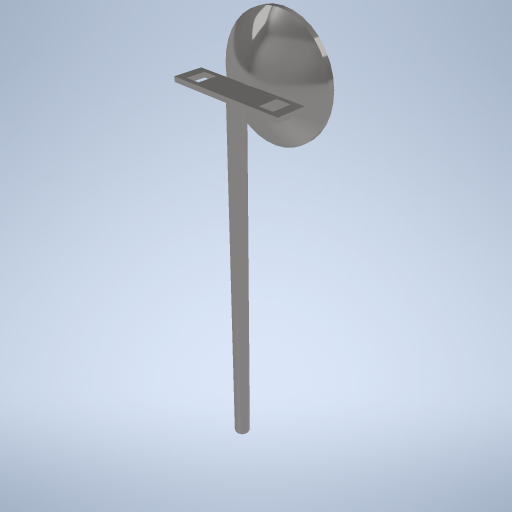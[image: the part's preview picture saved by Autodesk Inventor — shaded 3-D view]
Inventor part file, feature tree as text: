
AUTODESK INVENTOR PART (.ipt)
format: ipt  version: 2024 (Build 280153000, 153)  size: 368,128 bytes
history: native  units: mm
features: other x10, plane x3, extrude x2
ambient origin geometry x8: Origin, YZ Plane, XZ Plane, XY Plane, X Axis, Y Axis, Z Axis, Center Point
bodies: Solid1 (feature_tree)
feature tree (15):
  other  "pole_sketch"
  other  "pole_revolve"
  plane  "Work Plane1"
  other  "dish_support_sketch"
  extrude  "dish_support_extrude"  Depth=480.0mm
  plane  "Work Plane2"
  other  "dish_sketch"
  other  "dish_revolve"
  plane  "Work Plane4"
  other  "interior_antenna_sketch"
  other  "interior_antenna_revolve"
  other  "slot_sketch"
  extrude  "slot_extrude"  Depth=17.3mm
  other  "2D Equation Curve1"
  other  "2D Equation Curve3"
